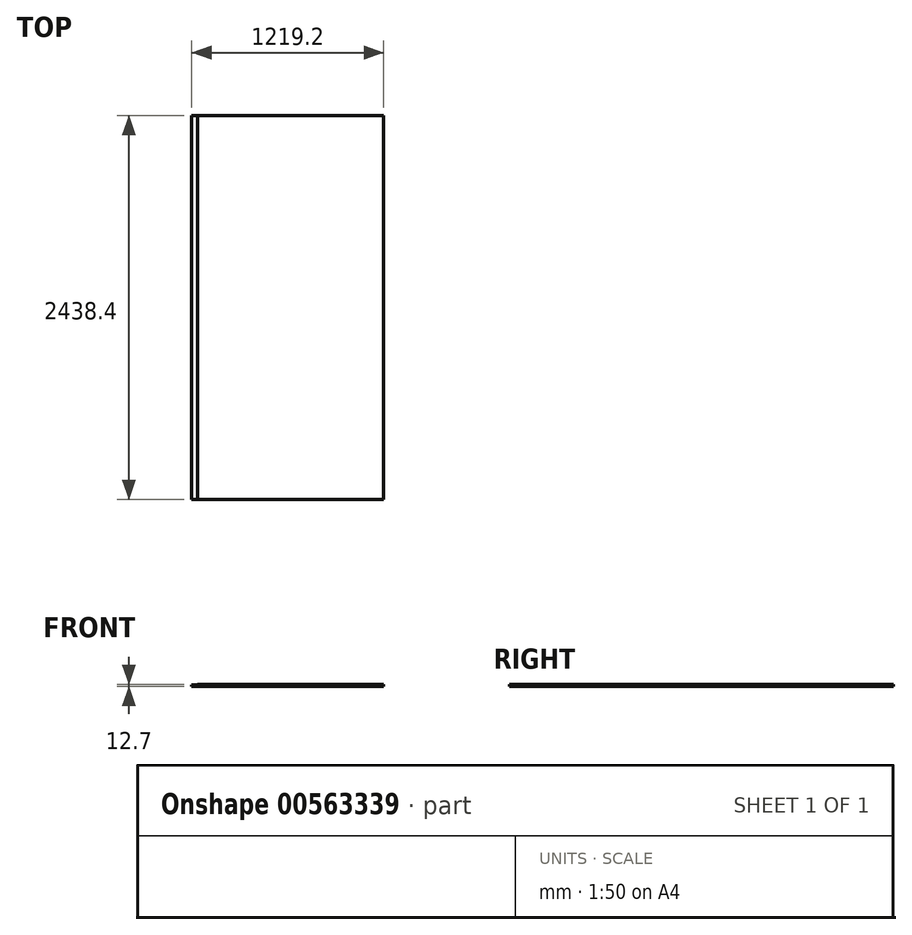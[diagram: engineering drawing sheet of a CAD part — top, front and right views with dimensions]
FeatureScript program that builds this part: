
annotation { "Feature Type Name" : "Feature", "Feature Type Description" : "" }
export const myFeature = defineFeature(function(context is Context, id is Id, definition is map)
    precondition{}
    {
        {
            var Q0;
            Q0=qCreatedBy(makeId("Front.planeOp"),FACE);
            var sketch = newSketch(context, id + "F0", { "sketchPlane" : qUnion([Q0])});
            skLineSegment(sketch, "E0.bottom", {"start": v(-609.6, -6.35) * mm, "end": v(609.6, -6.35) * mm});
            skLineSegment(sketch, "E0.top", {"start": v(-571.5, 6.35) * mm, "end": v(609.6, 6.35) * mm});
            skLineSegment(sketch, "E0.left", {"start": v(-609.6, -6.35) * mm, "end": v(-609.6, 3.18) * mm});
            skLineSegment(sketch, "E0.right", {"start": v(609.6, -6.35) * mm, "end": v(609.6, 6.35) * mm});
            skPoint(sketch, "E0.middle", {"position": v(0, 0) * mm});
            skLineSegment(sketch, "E1", {"start": v(-609.6, 3.18) * mm, "end": v(-571.5, 6.35) * mm});
            skPoint(sketch, "E2.orphan", {"position": v(-609.6, 6.35) * mm});
            skSolve(sketch);
        }
        {
            var Q0;
            Q0 = qSketchRegion(id + "F0", true);
            extrude(context, id + "F1", {"entities" : qUnion([Q0]), "depth" : 2438.4 * mm, "offsetDistance" : 25.4 * mm});
        }
    });
